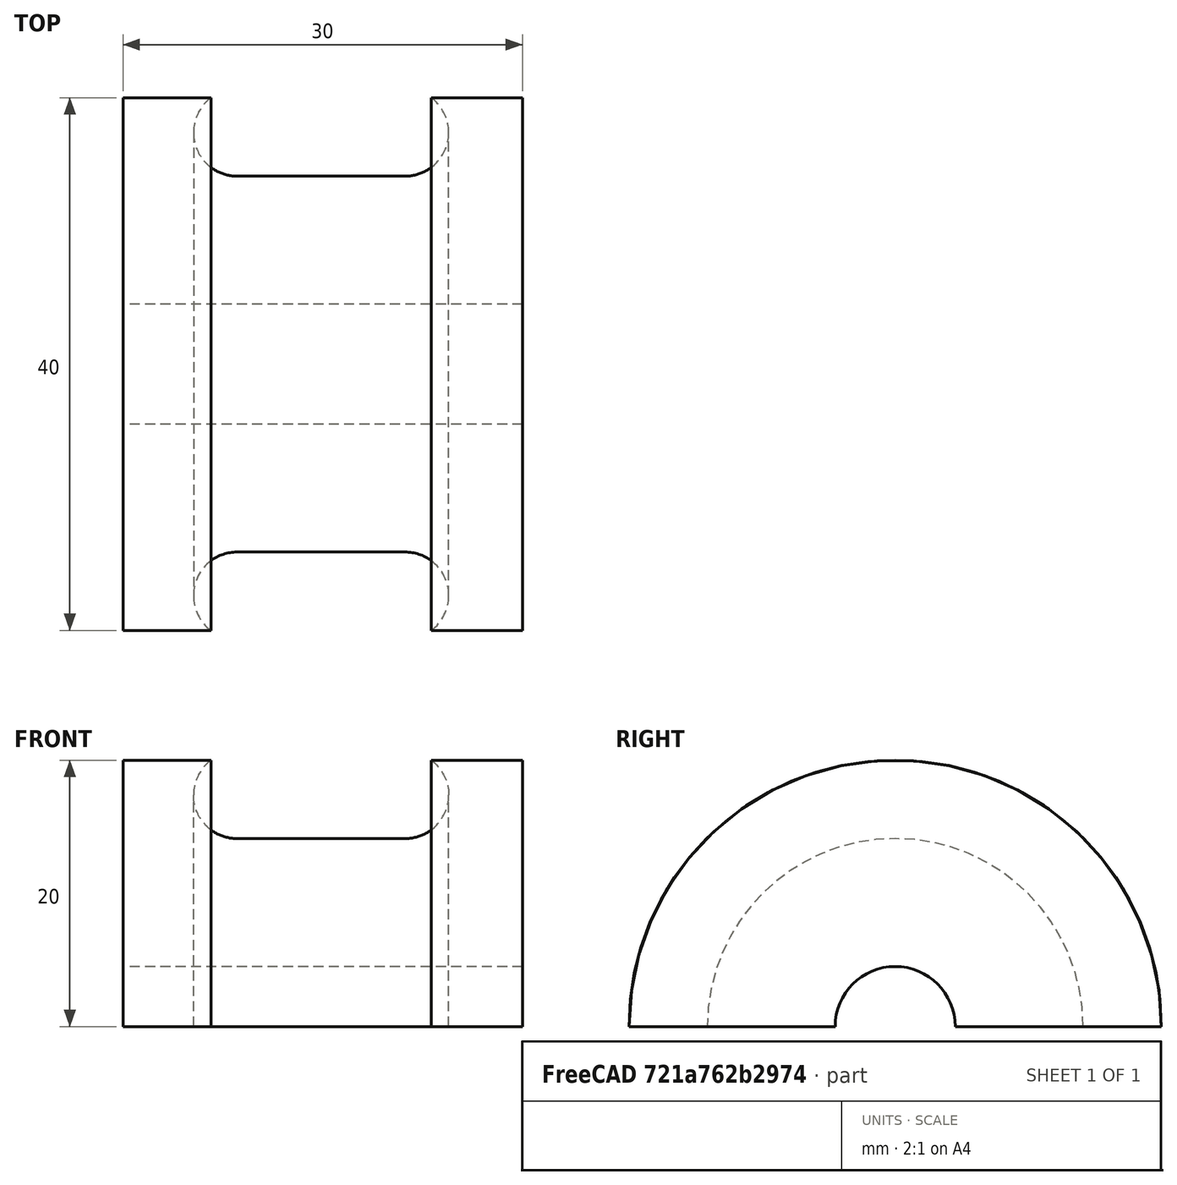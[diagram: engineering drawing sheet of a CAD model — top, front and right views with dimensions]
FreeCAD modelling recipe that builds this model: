
FCSTD DOCUMENT  (FreeCAD 0.17R13541 (Git))
Label: testFreeCad4
License: All rights reserved
LicenseURL: http://en.wikipedia.org/wiki/All_rights_reserved
objects: Sketcher::SketchObject×2, PartDesign::Revolution×1, PartDesign::Groove×1, PartDesign::Body×1
note: 7 computed .brp shape members not serialized (recipe doc carries the construction recipe); baked Part::Feature solids carry a one-line shape summary decoded from their .brp

FEATURE [Sketcher::SketchObject] Sketch
  MapMode = 5
  Support = -> [XY_Plane]
  sketch-geometry (4):
    g0: LineSegment StartX=5.14399 StartY=20 StartZ=0 EndX=35.144 EndY=20 EndZ=0
    g1: LineSegment StartX=35.144 StartY=20 StartZ=0 EndX=35.144 EndY=4.50687 EndZ=0
    g2: LineSegment StartX=35.144 StartY=4.50687 StartZ=0 EndX=5.14399 EndY=4.50687 EndZ=0
    g3: LineSegment StartX=5.14399 StartY=4.50687 StartZ=0 EndX=5.14399 EndY=20 EndZ=0
  constraints (8):
    c: Coincident(g0,g1)
    c: Coincident(g1,g2)
    c: Coincident(g2,g3)
    c: Coincident(g3,g0)
    c: Horizontal(g0)
    c: Horizontal(g2)
    c: Vertical(g1)
    c: Vertical(g3)
FEATURE [PartDesign::Revolution] Revolution
  Angle = 180
  Axis = (1,0,0)
  Base = (0,0,0)
  Profile = -> Sketch
  ReferenceAxis = -> Sketch [H_Axis]
FEATURE [Sketcher::SketchObject] Sketch001
  MapMode = 5
  Placement = pos=(0,0,0) rot=(1,0,0;3.14159rad)
  Support = -> [Revolution]
  sketch-geometry (5):
    g0: ArcOfCircle CenterX=13.7085 CenterY=17.3869 CenterZ=0 NormalX=0 NormalY=0 NormalZ=1 AngleXU=0 Radius=3.27327 StartAngle=1.5708 EndAngle=4.71239
    g1: ArcOfCircle CenterX=26.3274 CenterY=17.3869 CenterZ=0 NormalX=0 NormalY=0 NormalZ=1 AngleXU=0 Radius=3.27327 StartAngle=4.71239 EndAngle=7.85398
    g2: LineSegment StartX=13.7085 StartY=14.1136 StartZ=0 EndX=26.3274 EndY=14.1136 EndZ=0
    g3: LineSegment StartX=13.7085 StartY=20.6601 StartZ=0 EndX=26.3274 EndY=20.6601 EndZ=0
    g4: LineSegment [constr] StartX=-7.29464 StartY=-23.7113 StartZ=0 EndX=47.2946 EndY=30.878 EndZ=0
  constraints (7):
    c: Tangent(g0,g3) = 1.5708
    c: Tangent(g0,g2) = -1.5708
    c: Tangent(g2,g1) = -1.5708
    c: Tangent(g3,g1) = 1.5708
    c: Horizontal(g2)
    c: Equal(g0,g1)
    c: Angle(g-1,g4) = 0.785398
FEATURE [PartDesign::Groove] Groove
  Angle = 360
  Axis = (1,0,0)
  Base = (0,0,0)
  BaseFeature = -> Revolution
  Profile = -> Sketch001
  ReferenceAxis = -> Sketch001 [H_Axis]
  Reversed = true
FEATURE [PartDesign::Body] Body
  Group = -> [Sketch,Revolution,Sketch001,Groove]
  Origin = -> Origin
  Tip = -> Groove
